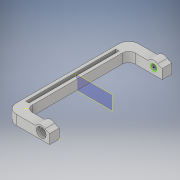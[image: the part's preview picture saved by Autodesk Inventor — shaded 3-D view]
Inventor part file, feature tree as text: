
AUTODESK INVENTOR PART (.ipt)
format: ipt  version: 2018 (Build 220112000, 112)  size: 231,936 bytes
history: native  units: in
note: dims shown in document units (in); Inventor stores cm internally (conversion verified against a paired STEP export)
features: sketch x17, extrude x10, fillet x6, hole x2, plane x1, mirror x1
ambient origin geometry x8: Origin, YZ Plane, XZ Plane, XY Plane, X Axis, Y Axis, Z Axis, Center Point
bodies: Solid1 (feature_tree)
feature tree (37):
  extrude  "Extrusion1"  Depth=0.375in
  sketch  "Sketch2"  dims[d3=0.375in d4=0.5in d5=0.375in d6=0.0in]
  extrude  "Extrusion2"  Depth=0.375in
  fillet  "Fillet1"  Radius=0.375in
  extrude  "Extrusion3"  Depth=0.375in
  extrude  "Extrusion4"  Depth=0.25in
  plane  "Work Plane1"
  mirror  "Mirror1"
  fillet  "Fillet2"  Radius=0.24in
  extrude  "Extrusion5"  Depth=0.375in
  sketch  "Sketch6"  dims[d17=1.0in d18=0.0in d19=0.24in d20=0.0in]
  extrude  "Extrusion6"  Depth=0.24in TaperAngle=0.0deg
  extrude  "Extrusion7"  Depth=0.375in
  fillet  "Fillet3"  Radius=0.25in
  fillet  "Fillet4"  Radius=0.375in
  fillet  "Fillet5"  Radius=0.25in
  fillet  "Fillet6"  Radius=0.125in
  sketch  "Sketch9"  dims[d30=0.125in d31=0.125in]
  extrude  "Extrusion8"  Depth=0.035in
  sketch  "Sketch11"  dims[d35=0.2in]
  sketch  "Sketch12"  dims[d36=0.2in d37=0.75in d38=0.375in d39=0.25in d40=0.5635in d41=0.35in d42=0.0in]
  hole  "Hole1"  [1 undecoded]
  hole  "Hole2"  [1 undecoded]
  sketch  "Sketch14"  dims[d51=3.5in d52=0.375in d53=0.0in]
  extrude  "Extrusion9"  Depth=0.125in
  extrude  "Extrusion10"  Depth=0.375in TaperAngle=0.0deg
  sketch  "Sketch17"
  sketch  "Sketch1"  dims[d0=1.3in d1=0.375in]
  sketch  "Sketch3"  dims[d7=0.375in d8=0.0in d9=0.375in]
  sketch  "Sketch4"  dims[d10=0.24in d11=0.0in d12=0.25in d13=0.24in d14=0.0in]
  sketch  "Sketch5"  dims[d15=2.0in d16=0.375in]
  sketch  "Sketch7"  dims[d21=0.375in d22=0.0in d23=0.375in d24=0.25in d25=0.375in d26=0.25in d27=0.125in]
  sketch  "Sketch8"  dims[d28=0.035in d29=0.035in]
  sketch  "Sketch10"  dims[d32=4.375in d33=0.0in d34=0.2in]
  sketch  "Sketch13"  dims[d43=0.2in d44=0.75in d45=0.375in d46=0.25in d47=0.5635in d48=0.35in d49=0.0in d50=0.125in]
  sketch  "Sketch15"  dims[d54=1.0in d55=0.0in]
  sketch  "Sketch16"
note: 2 required parameter values undecoded (feature->parameter linkage not recoverable at this tier; creation-order binding heuristic only, values carry confidence <= 0.55)
